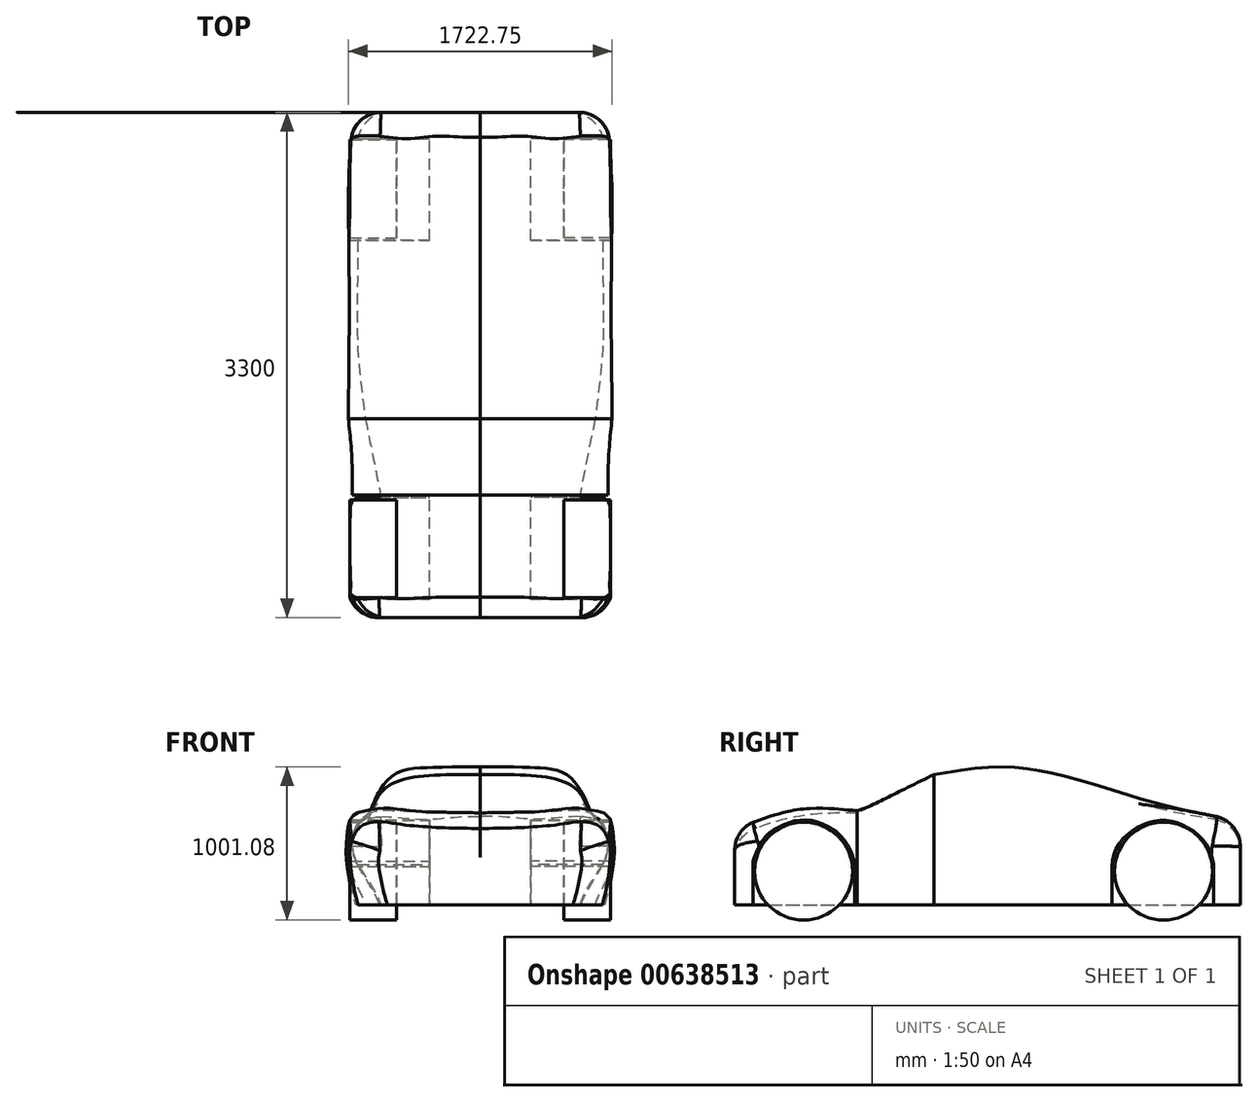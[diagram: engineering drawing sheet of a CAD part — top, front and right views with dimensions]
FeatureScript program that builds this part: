
annotation { "Feature Type Name" : "Feature", "Feature Type Description" : "" }
export const myFeature = defineFeature(function(context is Context, id is Id, definition is map)
    precondition{}
    {
        {
            var Q0;
            Q0=qCreatedBy(makeId("Front.planeOp"),FACE);
            cPlane(context, id + "F0", {"entities" : qUnion([Q0]), "cplaneType" : CPlaneType.OFFSET, "offset" : 500 * mm, "width" : 150 * mm, "height" : 150 * mm});
        }
        {
            var Q0;
            Q0=qCreatedBy(makeId("Front.planeOp"),FACE);
            cPlane(context, id + "F1", {"entities" : qUnion([Q0]), "cplaneType" : CPlaneType.OFFSET, "offset" : 1000 * mm, "width" : 150 * mm, "height" : 150 * mm});
        }
        {
            var Q0;
            Q0=qCreatedBy(makeId("Front.planeOp"),FACE);
            cPlane(context, id + "F2", {"entities" : qUnion([Q0]), "cplaneType" : CPlaneType.OFFSET, "offset" : 500 * mm, "oppositeDirection" : true, "width" : 150 * mm, "height" : 150 * mm});
        }
        {
            var Q0;
            Q0=qCreatedBy(makeId("Front.planeOp"),FACE);
            cPlane(context, id + "F3", {"entities" : qUnion([Q0]), "cplaneType" : CPlaneType.OFFSET, "offset" : 1000 * mm, "oppositeDirection" : true, "width" : 150 * mm, "height" : 150 * mm});
        }
        {
            var Q0;
            Q0=qCreatedBy(id+"F0.planeOp",FACE);
            var sketch = newSketch(context, id + "F4", { "sketchPlane" : qUnion([Q0])});
            skLineSegment(sketch, "E0", {"start": v(-329.43, -354.75) * mm, "end": v(420.57, -354.75) * mm});
            skFitSpline(sketch, "E1", {"points": [v(420.57, -354.75) * mm, v(520.3, -125.86) * mm, v(513.99, 71.53) * mm, v(449.54, 198.62) * mm, v(401.67, 233.61) * mm, v(333.2, 358.13) * mm, v(225.18, 446.35) * mm, v(30.74, 487.76) * mm, v(-329.43, 495.25) * mm], "startDerivative": vector(420, 1338.1) * mm, "endDerivative": vector(-2531.12, -27.95) * mm});
            skLineSegment(sketch, "E2", {"start": v(-329.43, 495.25) * mm, "end": v(-329.43, -354.75) * mm});
            skSolve(sketch);
        }
        {
            var Q0;
            Q0=qCreatedBy(id+"F1.planeOp",FACE);
            var sketch = newSketch(context, id + "F5", { "sketchPlane" : qUnion([Q0])});
            skLineSegment(sketch, "E3", {"start": v(-329.43, -354.75) * mm, "end": v(320.57, -354.75) * mm});
            skFitSpline(sketch, "E4", {"points": [v(320.57, -354.75) * mm, v(461.49, -103.35) * mm, v(504.14, 65.28) * mm, v(430.12, 217.42) * mm, v(323.95, 258.37) * mm, v(140.53, 254.14) * mm, v(-329.43, 245.25) * mm], "startDerivative": vector(420, 1338.1) * mm, "endDerivative": vector(-2650.38, -82.73) * mm});
            skLineSegment(sketch, "E5", {"start": v(-329.43, 245.25) * mm, "end": v(-329.43, -354.75) * mm});
            skSolve(sketch);
        }
        {
            var Q0;
            Q0=qCreatedBy(id+"F2.planeOp",FACE);
            var sketch = newSketch(context, id + "F6", { "sketchPlane" : qUnion([Q0])});
            skLineSegment(sketch, "E6", {"start": v(-329.43, -354.75) * mm, "end": v(470.57, -354.75) * mm});
            skFitSpline(sketch, "E7", {"points": [v(470.57, -354.75) * mm, v(520.3, -125.86) * mm, v(513.99, 71.53) * mm, v(449.54, 198.62) * mm, v(401.67, 233.61) * mm, v(324.2, 325.72) * mm, v(208.9, 398.28) * mm, v(41.54, 433.74) * mm, v(-329.43, 445.25) * mm], "startDerivative": vector(420, 1338.1) * mm, "endDerivative": vector(-3337.5, -18.3) * mm});
            skLineSegment(sketch, "E8", {"start": v(-329.43, 445.25) * mm, "end": v(-329.43, -354.75) * mm});
            skSolve(sketch);
        }
        {
            var Q0;
            Q0=qCreatedBy(id+"F3.planeOp",FACE);
            var sketch = newSketch(context, id + "F7", { "sketchPlane" : qUnion([Q0])});
            skLineSegment(sketch, "E9", {"start": v(-329.43, -354.75) * mm, "end": v(470.57, -354.75) * mm});
            skFitSpline(sketch, "E10", {"points": [v(470.57, -354.75) * mm, v(520.3, -125.86) * mm, v(527.68, 157.11) * mm, v(517.15, 214.52) * mm, v(488.3, 247.96) * mm, v(341.62, 282.77) * mm, v(163.59, 268.1) * mm, v(18.13, 286.11) * mm, v(-329.43, 295.25) * mm], "startDerivative": vector(420, 1338.1) * mm, "endDerivative": vector(-2531.12, -27.95) * mm});
            skLineSegment(sketch, "E11", {"start": v(-329.43, 295.25) * mm, "end": v(-329.43, -354.75) * mm});
            skSolve(sketch);
        }
        {
            var Q0;
            Q0=qCreatedBy(makeId("Front.planeOp"),FACE);
            cPlane(context, id + "F8", {"entities" : qUnion([Q0]), "cplaneType" : CPlaneType.OFFSET, "offset" : 25 * mm, "width" : 150 * mm, "height" : 150 * mm});
        }
        {
            var Q0;
            Q0=qCreatedBy(id+"F8.planeOp",FACE);
            var sketch = newSketch(context, id + "F9", { "sketchPlane" : qUnion([Q0])});
            skLineSegment(sketch, "E12", {"start": v(-329.43, -354.75) * mm, "end": v(470.57, -354.75) * mm});
            skFitSpline(sketch, "E13", {"points": [v(470.57, -354.75) * mm, v(520.3, -125.86) * mm, v(513.99, 71.53) * mm, v(449.54, 198.62) * mm, v(401.67, 233.61) * mm, v(353.8, 334.86) * mm, v(234.11, 495.05) * mm, v(51.83, 539.36) * mm, v(-329.43, 545.25) * mm], "startDerivative": vector(420, 1338.1) * mm, "endDerivative": vector(-2531.12, -27.95) * mm});
            skLineSegment(sketch, "E14", {"start": v(-329.43, 545.25) * mm, "end": v(-329.43, -354.75) * mm});
            skSolve(sketch);
        }
        {
            var Q0;
            Q0=qCreatedBy(makeId("Front.planeOp"),FACE);
            cPlane(context, id + "F10", {"entities" : qUnion([Q0]), "cplaneType" : CPlaneType.OFFSET, "offset" : 1800 * mm, "width" : 150 * mm, "height" : 150 * mm});
        }
        {
            var Q0;
            Q0=qCreatedBy(makeId("Front.planeOp"),FACE);
            cPlane(context, id + "F11", {"entities" : qUnion([Q0]), "cplaneType" : CPlaneType.OFFSET, "offset" : 1500 * mm, "oppositeDirection" : true, "width" : 150 * mm, "height" : 150 * mm});
        }
        {
            var Q0;
            Q0=qCreatedBy(id+"F10.planeOp",FACE);
            var sketch = newSketch(context, id + "F12", { "sketchPlane" : qUnion([Q0])});
            skLineSegment(sketch, "E15", {"start": v(-329.43, -354.75) * mm, "end": v(470.57, -354.75) * mm});
            skFitSpline(sketch, "E16", {"points": [v(470.57, -354.75) * mm, v(506.28, -117.83) * mm, v(481.58, 0) * mm, v(382.76, 129.2) * mm, v(208.12, 120.29) * mm, v(38.1, 105.3) * mm, v(-329.43, 95.25) * mm], "startDerivative": vector(372.09, 1480.21) * mm, "endDerivative": vector(-2531.12, -27.95) * mm});
            skLineSegment(sketch, "E17", {"start": v(-329.43, 95.25) * mm, "end": v(-329.43, -354.75) * mm});
            skSolve(sketch);
        }
        {
            var Q0;
            Q0=qCreatedBy(id+"F11.planeOp",FACE);
            var sketch = newSketch(context, id + "F13", { "sketchPlane" : qUnion([Q0])});
            skLineSegment(sketch, "E18", {"start": v(-329.43, -354.75) * mm, "end": v(470.57, -354.75) * mm});
            skFitSpline(sketch, "E19", {"points": [v(470.57, -354.75) * mm, v(502, -129.78) * mm, v(482.2, 62.86) * mm, v(409.94, 148.96) * mm, v(325.95, 181.08) * mm, v(156.33, 187.1) * mm, v(-56.96, 173.67) * mm, v(-329.43, 195.25) * mm], "startDerivative": vector(420, 1338.1) * mm, "endDerivative": vector(-2531.12, -27.95) * mm});
            skLineSegment(sketch, "E20", {"start": v(-329.43, 195.25) * mm, "end": v(-329.43, -354.75) * mm});
            skSolve(sketch);
        }
        {
            var Q0;
            Q0=qCreatedBy(makeId("Right.planeOp"),FACE);
            var sketch = newSketch(context, id + "F14", { "sketchPlane" : qUnion([Q0])});
            skLineSegment(sketch, "E21", {"start": v(-1680.44, -386.84) * mm, "end": v(-1680.44, -68.04) * mm});
            skFitSpline(sketch, "E22", {"points": [v(-1680.44, -68.04) * mm, v(-1641.42, 27.64) * mm, v(-1567.37, 119.12) * mm, v(-1345.2, 200.44) * mm, v(-1153.52, 133.64) * mm, v(-1067.85, 45.06) * mm, v(-1017.02, -92.89) * mm], "startDerivative": vector(249.19, 819.5) * mm, "endDerivative": vector(156.56, -965.44) * mm});
            skLineSegment(sketch, "E23", {"start": v(-1017.02, -92.89) * mm, "end": v(-1017.02, -393.51) * mm});
            skLineSegment(sketch, "E24", {"start": v(-1017.02, -393.51) * mm, "end": v(-1680.44, -386.84) * mm});
            skSolve(sketch);
        }
        {
            var Q0;
            Q0=qCreatedBy(makeId("Right.planeOp"),FACE);
            var sketch = newSketch(context, id + "F15", { "sketchPlane" : qUnion([Q0])});
            skLineSegment(sketch, "E25", {"start": v(663.28, -368.71) * mm, "end": v(663.28, -103.41) * mm});
            skFitSpline(sketch, "E26", {"points": [v(663.28, -103.41) * mm, v(743.75, 87.03) * mm, v(995.8, 197.34) * mm, v(1233.5, 94.27) * mm, v(1327.6, -103.41) * mm], "startDerivative": vector(-14.88, 899.96) * mm, "endDerivative": vector(102.88, -1030.05) * mm});
            skLineSegment(sketch, "E27", {"start": v(1327.6, -103.41) * mm, "end": v(1327.6, -368.71) * mm});
            skLineSegment(sketch, "E28", {"start": v(1327.6, -368.71) * mm, "end": v(663.28, -368.71) * mm});
            skSolve(sketch);
        }
        {
            var Q0;
            Q0=qCreatedBy(makeId("Front.planeOp"),FACE);
            cPlane(context, id + "F16", {"entities" : qUnion([Q0]), "cplaneType" : CPlaneType.OFFSET, "offset" : 1400 * mm, "width" : 150 * mm, "height" : 150 * mm});
        }
        {
            var Q0;
            Q0=qCreatedBy(id+"F16.planeOp",FACE);
            var sketch = newSketch(context, id + "F17", { "sketchPlane" : qUnion([Q0])});
            skLineSegment(sketch, "E29", {"start": v(-329.43, -354.75) * mm, "end": v(470.57, -354.75) * mm});
            skFitSpline(sketch, "E30", {"points": [v(470.57, -354.75) * mm, v(536.12, -93.18) * mm, v(543.8, 55.27) * mm, v(507.97, 219.08) * mm, v(420.94, 254.91) * mm, v(277.6, 265.15) * mm, v(141.95, 249.8) * mm, v(-58.23, 225.89) * mm, v(-329.43, 220.25) * mm], "startDerivative": vector(420, 1338.1) * mm, "endDerivative": vector(-2531.12, -27.95) * mm});
            skLineSegment(sketch, "E31", {"start": v(-329.43, 220.25) * mm, "end": v(-329.43, -354.75) * mm});
            skSolve(sketch);
        }
        {
            var Q0;
            Q0=makeQuery(id+"F13.imprint","IMPRINT",FACE,{"disambiguationData":[TD([[makeQuery(id+"F13.imprint","IMPRINT",EDGE,{"derivedFrom":sQuery(id+"F13.wireOp",EDGE,"E18")}),1.0]])]});
            var Q1;
            Q1=makeQuery(id+"F7.imprint","IMPRINT",FACE,{"disambiguationData":[TD([[makeQuery(id+"F7.imprint","IMPRINT",EDGE,{"derivedFrom":sQuery(id+"F7.wireOp",EDGE,"E9")}),1.0]])]});
            var Q2;
            Q2=makeQuery(id+"F6.imprint","IMPRINT",FACE,{"disambiguationData":[TD([[makeQuery(id+"F6.imprint","IMPRINT",EDGE,{"derivedFrom":sQuery(id+"F6.wireOp",EDGE,"E6")}),1.0]])]});
            var Q3;
            Q3=makeQuery(id+"F9.imprint","IMPRINT",FACE,{"disambiguationData":[TD([[makeQuery(id+"F9.imprint","IMPRINT",EDGE,{"derivedFrom":sQuery(id+"F9.wireOp",EDGE,"E12")}),1.0]])]});
            var Q4;
            Q4=makeQuery(id+"F4.imprint","IMPRINT",FACE,{"disambiguationData":[TD([[makeQuery(id+"F4.imprint","IMPRINT",EDGE,{"derivedFrom":sQuery(id+"F4.wireOp",EDGE,"E0")}),1.0]])]});
            loft(context, id + "F18", {"sheetProfilesArray" : [{ "sheetProfileEntities" : qUnion([Q0]) }, { "sheetProfileEntities" : qUnion([Q1]) }, { "sheetProfileEntities" : qUnion([Q2]) }, { "sheetProfileEntities" : qUnion([Q3]) }, { "sheetProfileEntities" : qUnion([Q4]) }]});
        }
        {
            var Q1;
            Q1=makeQuery(id+"F4.imprint","IMPRINT",FACE,{"disambiguationData":[TD([[makeQuery(id+"F4.imprint","IMPRINT",EDGE,{"derivedFrom":sQuery(id+"F4.wireOp",EDGE,"E0")}),1.0]])]});
            var Q2;
            Q2=makeQuery(id+"F5.imprint","IMPRINT",FACE,{"disambiguationData":[TD([[makeQuery(id+"F5.imprint","IMPRINT",EDGE,{"derivedFrom":sQuery(id+"F5.wireOp",EDGE,"E3")}),1.0]])]});
            loft(context, id + "F19", {"operationType" : NewBodyOperationType.ADD, "sheetProfilesArray" : [{ "sheetProfileEntities" : qUnion([Q1]) }, { "sheetProfileEntities" : qUnion([Q2]) }]});
        }
        {
            var Q1;
            Q1=makeQuery(id+"F5.imprint","IMPRINT",FACE,{"disambiguationData":[TD([[makeQuery(id+"F5.imprint","IMPRINT",EDGE,{"derivedFrom":sQuery(id+"F5.wireOp",EDGE,"E3")}),1.0]])]});
            var Q2;
            Q2=makeQuery(id+"F17.imprint","IMPRINT",FACE,{"disambiguationData":[TD([[makeQuery(id+"F17.imprint","IMPRINT",EDGE,{"derivedFrom":sQuery(id+"F17.wireOp",EDGE,"E29")}),1.0]])]});
            var Q3;
            Q3=makeQuery(id+"F12.imprint","IMPRINT",FACE,{"disambiguationData":[TD([[makeQuery(id+"F12.imprint","IMPRINT",EDGE,{"derivedFrom":sQuery(id+"F12.wireOp",EDGE,"E15")}),1.0]])]});
            loft(context, id + "F20", {"operationType" : NewBodyOperationType.ADD, "sheetProfilesArray" : [{ "sheetProfileEntities" : qUnion([Q1]) }, { "sheetProfileEntities" : qUnion([Q2]) }, { "sheetProfileEntities" : qUnion([Q3]) }]});
        }
        {
            var Q0;
            {var subQ0=sQuery(id+"F13.wireOp",EDGE,"E19");var subQ1=sQuery(id+"F13.wireOp",EDGE,"E20");var subQ2=sQuery(id+"F13.wireOp",EDGE,"E18");Q0=makeQuery(id+"F18.opLoft","MID_CAP_EDGE",EDGE,{"disambiguationData":[OSD([subQ2,subQ0,subQ1]),TDD([makeQuery(id+"F13.imprint","INTERSECT",VERTEX,{"derivedFrom":[subQ2,subQ0]}),makeQuery(id+"F13.imprint","INTERSECT",VERTEX,{"derivedFrom":[subQ0,subQ1]}),makeQuery(id+"F13.imprint","IMPRINT",EDGE,{"derivedFrom":subQ0})])],"capPos":0.0});}
            fillet(context, id + "F21", {"entities" : qUnion([Q0]), "radius" : 200 * mm, "tangentPropagation" : true, "allowEdgeOverflow" : false});
        }
        {
            var Q0;
            {var subQ0=sQuery(id+"F12.wireOp",EDGE,"E16");var subQ1=sQuery(id+"F12.wireOp",EDGE,"E17");var subQ2=sQuery(id+"F12.wireOp",EDGE,"E15");Q0=makeQuery(id+"F20.opLoft","MID_CAP_EDGE",EDGE,{"disambiguationData":[OSD([subQ2,subQ0,subQ1]),TDD([makeQuery(id+"F12.imprint","INTERSECT",VERTEX,{"derivedFrom":[subQ2,subQ0]}),makeQuery(id+"F12.imprint","INTERSECT",VERTEX,{"derivedFrom":[subQ0,subQ1]}),makeQuery(id+"F12.imprint","IMPRINT",EDGE,{"derivedFrom":subQ0})])],"capPos":2.0});}
            fillet(context, id + "F22", {"entities" : qUnion([Q0]), "radius" : 200 * mm, "tangentPropagation" : true, "allowEdgeOverflow" : false});
        }
        {
            var Q0;
            Q0=makeQuery(id+"F14.imprint","IMPRINT",FACE,{"disambiguationData":[TD([[makeQuery(id+"F14.imprint","IMPRINT",EDGE,{"derivedFrom":sQuery(id+"F14.wireOp",EDGE,"E21")}),-1.0]])]});
            extrude(context, id + "F23", {"entities" : qUnion([Q0]), "operationType" : NewBodyOperationType.REMOVE, "depth" : 600 * mm, "offsetDistance" : 25 * mm});
        }
        {
            var Q0;
            Q0=makeQuery(id+"F15.imprint","IMPRINT",FACE,{"disambiguationData":[TD([[makeQuery(id+"F15.imprint","IMPRINT",EDGE,{"derivedFrom":sQuery(id+"F15.wireOp",EDGE,"E25")}),-1.0]])]});
            extrude(context, id + "F24", {"entities" : qUnion([Q0]), "operationType" : NewBodyOperationType.REMOVE, "depth" : 600 * mm, "offsetDistance" : 25 * mm});
        }
        {
            var Q0;
            Q0=qCreatedBy(makeId("Front.planeOp"),FACE);
            cPlane(context, id + "F25", {"entities" : qUnion([Q0]), "cplaneType" : CPlaneType.OFFSET, "offset" : 1350 * mm, "width" : 150 * mm, "height" : 150 * mm});
        }
        {
            var Q0;
            Q0=qCreatedBy(id+"F25.planeOp",FACE);
            var sketch = newSketch(context, id + "F26", { "sketchPlane" : qUnion([Q0])});
            skLineSegment(sketch, "E32.bottom", {"start": v(215.57, -454.75) * mm, "end": v(520.57, -454.75) * mm});
            skLineSegment(sketch, "E32.top", {"start": v(215.57, -134.75) * mm, "end": v(520.57, -134.75) * mm});
            skLineSegment(sketch, "E32.left", {"start": v(215.57, -454.75) * mm, "end": v(215.57, -134.75) * mm});
            skLineSegment(sketch, "E32.right", {"start": v(520.57, -454.75) * mm, "end": v(520.57, -134.75) * mm});
            skSolve(sketch);
        }
        {
            var Q0;
            Q0=makeQuery(id+"F26.imprint","IMPRINT",FACE,{"disambiguationData":[TD([[makeQuery(id+"F26.imprint","IMPRINT",EDGE,{"derivedFrom":sQuery(id+"F26.wireOp",EDGE,"E32.bottom")}),1.0]])]});
            var Q1;
            Q1=sQuery(id+"F26.wireOp",EDGE,"E32.top");
            revolve(context, id + "F27", {"operationType" : NewBodyOperationType.ADD, "entities" : qUnion([Q0]), "axis" : qUnion([Q1]), "revolveType" : RevolveType.FULL});
        }
        {
            var Q0;
            Q0=qCreatedBy(makeId("Front.planeOp"),FACE);
            cPlane(context, id + "F28", {"entities" : qUnion([Q0]), "cplaneType" : CPlaneType.OFFSET, "offset" : 1000 * mm, "oppositeDirection" : true, "width" : 150 * mm, "height" : 150 * mm});
        }
        {
            var Q0;
            Q0=qCreatedBy(id+"F28.planeOp",FACE);
            var sketch = newSketch(context, id + "F29", { "sketchPlane" : qUnion([Q0])});
            skLineSegment(sketch, "E33.bottom", {"start": v(215.57, -134.75) * mm, "end": v(520.57, -134.75) * mm});
            skLineSegment(sketch, "E33.top", {"start": v(215.57, 185.25) * mm, "end": v(520.57, 185.25) * mm});
            skLineSegment(sketch, "E33.left", {"start": v(215.57, -134.75) * mm, "end": v(215.57, 185.25) * mm});
            skLineSegment(sketch, "E33.right", {"start": v(520.57, -134.75) * mm, "end": v(520.57, 185.25) * mm});
            skSolve(sketch);
        }
        {
            var Q0;
            Q0=makeQuery(id+"F29.imprint","IMPRINT",FACE,{"disambiguationData":[TD([[makeQuery(id+"F29.imprint","IMPRINT",EDGE,{"derivedFrom":sQuery(id+"F29.wireOp",EDGE,"E33.bottom")}),1.0]])]});
            var Q1;
            Q1=sQuery(id+"F29.wireOp",EDGE,"E33.bottom");
            revolve(context, id + "F30", {"operationType" : NewBodyOperationType.ADD, "entities" : qUnion([Q0]), "axis" : qUnion([Q1]), "revolveType" : RevolveType.FULL});
        }
        {
            var Q0;
            Q0=makeQuery(id+"F18.opLoft","SWEPT_BODY",BODY,{"disambiguationData":[OSD([makeQuery(id+"F4.imprint","IMPRINT",FACE,{"disambiguationData":[TD([[makeQuery(id+"F4.imprint","IMPRINT",EDGE,{"derivedFrom":sQuery(id+"F4.wireOp",EDGE,"E0")}),1.0]])]}),sQuery(id+"F6.wireOp",EDGE,"E8"),sQuery(id+"F7.wireOp",EDGE,"E11"),sQuery(id+"F9.wireOp",EDGE,"E14"),makeQuery(id+"F13.imprint","IMPRINT",FACE,{"disambiguationData":[TD([[makeQuery(id+"F13.imprint","IMPRINT",EDGE,{"derivedFrom":sQuery(id+"F13.wireOp",EDGE,"E18")}),1.0]])]})])]});
            var Q1;
            Q1=makeQuery(id+"F30.opRevolve","SWEPT_BODY",BODY,{"disambiguationData":[OSD([sQuery(id+"F29.wireOp",EDGE,"E33.bottom"),sQuery(id+"F29.wireOp",EDGE,"E33.top"),sQuery(id+"F29.wireOp",EDGE,"E33.left"),sQuery(id+"F29.wireOp",EDGE,"E33.right")])]});
            var Q2;
            Q2=makeQuery(id+"F27.opRevolve","SWEPT_BODY",BODY,{"disambiguationData":[OSD([sQuery(id+"F26.wireOp",EDGE,"E32.bottom"),sQuery(id+"F26.wireOp",EDGE,"E32.top"),sQuery(id+"F26.wireOp",EDGE,"E32.left"),sQuery(id+"F26.wireOp",EDGE,"E32.right")])]});
            var Q3;
            {var subQ0=sQuery(id+"F17.wireOp",EDGE,"E31");var subQ1=sQuery(id+"F17.wireOp",EDGE,"E30");var subQ2=sQuery(id+"F17.wireOp",EDGE,"E29");var subQ3=sQuery(id+"F5.wireOp",EDGE,"E5");var subQ4=makeQuery(id+"F5.imprint","IMPRINT",EDGE,{"derivedFrom":subQ3});var subQ5=sQuery(id+"F5.wireOp",EDGE,"E4");var subQ6=makeQuery(id+"F5.imprint","INTERSECT",VERTEX,{"derivedFrom":[subQ5,subQ3]});var subQ7=sQuery(id+"F5.wireOp",EDGE,"E3");var subQ8=makeQuery(id+"F5.imprint","INTERSECT",VERTEX,{"derivedFrom":[subQ7,subQ3]});var subQ9=sQuery(id+"F4.wireOp",EDGE,"E2");var subQ10=sQuery(id+"F4.wireOp",EDGE,"E1");var subQ11=sQuery(id+"F4.wireOp",EDGE,"E0");var subQ12=sQuery(id+"F13.wireOp",EDGE,"E20");var subQ13=sQuery(id+"F13.wireOp",EDGE,"E19");var subQ14=sQuery(id+"F13.wireOp",EDGE,"E18");var subQ15=sQuery(id+"F7.wireOp",EDGE,"E11");var subQ16=sQuery(id+"F7.wireOp",EDGE,"E10");var subQ17=sQuery(id+"F7.wireOp",EDGE,"E9");Q3=makeQuery(id+"F20.boolean.opBoolean","MERGE",FACE,{"derivedFrom":[makeQuery(id+"F19.boolean.opBoolean","MERGE",FACE,{"derivedFrom":[makeQuery(id+"F18.opLoft","SWEPT_FACE",FACE,{"disambiguationData":[OSD([subQ17,subQ16,subQ15,subQ14,subQ13,subQ12]),TDD([makeQuery(id+"F7.imprint","INTERSECT",VERTEX,{"derivedFrom":[subQ17,subQ15]}),makeQuery(id+"F7.imprint","INTERSECT",VERTEX,{"derivedFrom":[subQ16,subQ15]}),makeQuery(id+"F7.imprint","IMPRINT",EDGE,{"derivedFrom":subQ15}),makeQuery(id+"F13.imprint","INTERSECT",VERTEX,{"derivedFrom":[subQ14,subQ12]}),makeQuery(id+"F13.imprint","INTERSECT",VERTEX,{"derivedFrom":[subQ13,subQ12]}),makeQuery(id+"F13.imprint","IMPRINT",EDGE,{"derivedFrom":subQ12})])]}),makeQuery(id+"F19.opLoft","SWEPT_FACE",FACE,{"disambiguationData":[OSD([subQ11,subQ10,subQ9,subQ7,subQ5,subQ3]),TDD([makeQuery(id+"F4.imprint","INTERSECT",VERTEX,{"derivedFrom":[subQ11,subQ9]}),makeQuery(id+"F4.imprint","INTERSECT",VERTEX,{"derivedFrom":[subQ10,subQ9]}),makeQuery(id+"F4.imprint","IMPRINT",EDGE,{"derivedFrom":subQ9}),subQ8,subQ6,subQ4])]})]}),makeQuery(id+"F20.opLoft","SWEPT_FACE",FACE,{"disambiguationData":[OSD([subQ7,subQ5,subQ3,subQ2,subQ1,subQ0]),TDD([subQ8,subQ6,subQ4,makeQuery(id+"F17.imprint","INTERSECT",VERTEX,{"derivedFrom":[subQ2,subQ0]}),makeQuery(id+"F17.imprint","INTERSECT",VERTEX,{"derivedFrom":[subQ1,subQ0]}),makeQuery(id+"F17.imprint","IMPRINT",EDGE,{"derivedFrom":subQ0})])]})]});}
            mirror(context, id + "F31", {"operationType" : NewBodyOperationType.ADD, "entities" : qUnion([Q0, Q1, Q2]), "mirrorPlane" : qUnion([Q3])});
        }
    });
